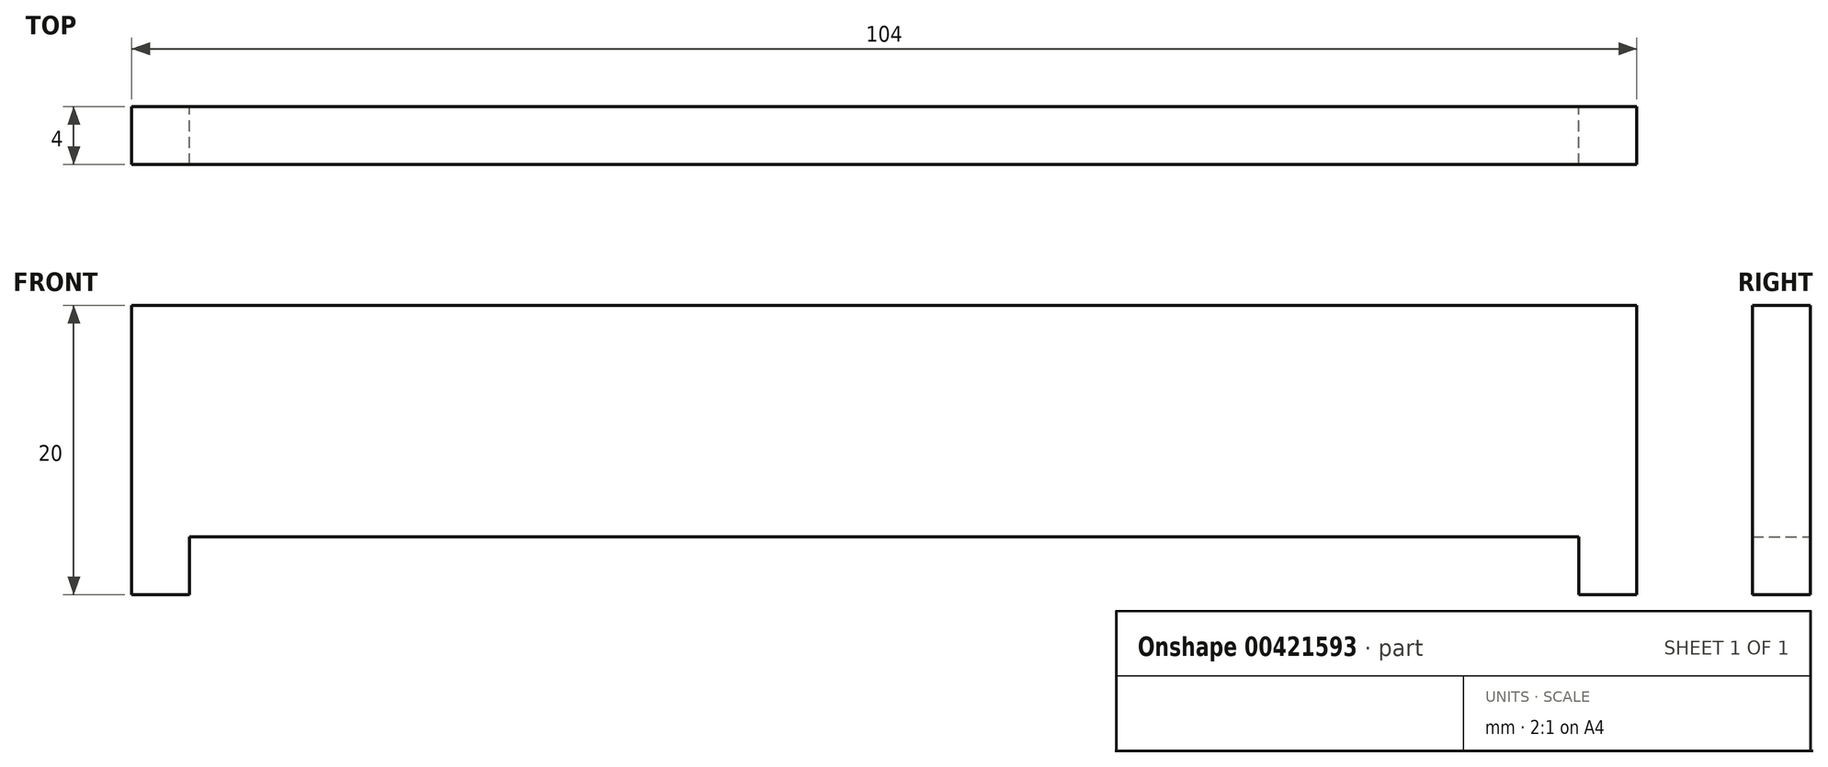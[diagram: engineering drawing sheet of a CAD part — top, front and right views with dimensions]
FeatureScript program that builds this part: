
annotation { "Feature Type Name" : "Feature", "Feature Type Description" : "" }
export const myFeature = defineFeature(function(context is Context, id is Id, definition is map)
    precondition{}
    {
        {
            var Q0;
            Q0=qCreatedBy(makeId("Front.planeOp"),FACE);
            var sketch = newSketch(context, id + "F0", { "sketchPlane" : qUnion([Q0])});
            skLineSegment(sketch, "E0", {"start": v(62.5, 13.75) * mm, "end": v(62.5, -6.25) * mm});
            skLineSegment(sketch, "E1", {"start": v(62.5, -6.25) * mm, "end": v(58.5, -6.25) * mm});
            skLineSegment(sketch, "E2", {"start": v(58.5, -6.25) * mm, "end": v(58.5, -2.25) * mm});
            skLineSegment(sketch, "E3", {"start": v(58.5, -2.25) * mm, "end": v(-37.5, -2.25) * mm});
            skLineSegment(sketch, "E4", {"start": v(-37.5, -2.25) * mm, "end": v(-37.5, -6.25) * mm});
            skLineSegment(sketch, "E5", {"start": v(-37.5, -6.25) * mm, "end": v(-41.5, -6.25) * mm});
            skLineSegment(sketch, "E6", {"start": v(-41.5, 13.75) * mm, "end": v(62.5, 13.75) * mm});
            skLineSegment(sketch, "E7", {"start": v(-41.5, 13.75) * mm, "end": v(-41.5, -6.25) * mm});
            skSolve(sketch);
        }
        {
            var Q0;
            Q0=makeQuery(id+"F0.imprint","IMPRINT",FACE,{"disambiguationData":[TD([[makeQuery(id+"F0.imprint","IMPRINT",EDGE,{"derivedFrom":sQuery(id+"F0.wireOp",EDGE,"E0")}),-1.0]])]});
            extrude(context, id + "F1", {"entities" : qUnion([Q0]), "depth" : 4 * mm, "offsetDistance" : 25 * mm});
        }
    });
